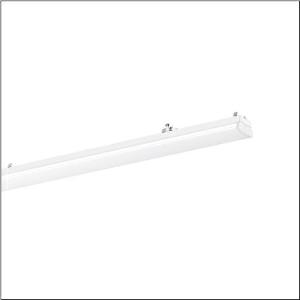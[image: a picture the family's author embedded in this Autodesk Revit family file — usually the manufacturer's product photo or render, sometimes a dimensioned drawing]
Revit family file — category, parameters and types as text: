
# Revit family: licross_r__11_recessed_opal_mo_51tl1ddv4e5g_e7a4
name_source: partatom
category: Lighting Fixtures
units: mm (PartAtom-declared; Revit-internal decimal feet)

## family parameters
Cut with Voids When Loaded = No
Host = Face
Light Source = No
Part Type = Normal
Room Calculation Point = No
Round Connector Dimension = Use Diameter
Shared = No

## types (1)
- --- (1 x LED, 14560 lm, 84.1 W, 4000K)
    Apparent Load = 84 VA
    CIE Flux Codes = 44 73 91 87 100
    Color Rendering = 80
    Color Temperature = 4000K
    Default Elevation = 1800 mm
    Description = Licross® 11 recessed opal MO, luminaire insert, of sheet steel, coil coated, white, length: 2.250mm, width: 76mm, height: 87mm, LED rated luminous flux: 14.560lm, light colour: 840, control gear: DALI 2, with plug, 5-pole, with phase selection, mains connection: 220..240V, AC, 50/60Hz, rated input power: 84W, halogen-free wiring, primary optical cover: cover, of PMMA, light emission: direct with ceiling illumination distribution, primary light characteristic: symmetric, protection rating (complete): IP40, insulation class (complete): insulation class I (protective earthing), certification: CE, ENEC, VDE, UKCA, protection symbol: D if used in an environment without relevant dust loads with corresponding accessories, impact resistance: IK06, permissible ambient temperature for indoor applications: -25..+35°C, corresponds to IFS (International Featured Standards) requirements for safety and quality in the food industry, reducing of maximum allowable ambient temperature of 5°C with ceiling mounting, LABS conformity tested according to VDMA 24364:2018-05, packaging unit: 1 piece
    Height = 83 mm
    Lamp = 1 x LED
    Lamp Light Flux = 14560 lm
    Lamp Power = 84.1 W
    Lamp count = 1
    Length = 2250 mm
    Luminous efficacy = 173 lm/W
    Manufacturer = Siteco
    ModVariant = No
    Model = 51TL1DDV4E5G
    Mounting Place = Ceiling
    Mounting Type = Pendant
    Number of Poles = 1
    OnlyDefault = Yes
    Power Factor = 1
    Product Name = Licross® 11 recessed opal MO
    Product group = luminaire insert
    ProductGroupID = 901
    Protection Class = Protection class I
    Protection Degree = IP 40
    RLX_Detail_Level = 1
    RLX_Emergency_Light_Flux = 0 lm
    RLX_Emergency_Type = 0
    RLX_Emergency_Type_DB = No
    RlxData = <blob elided: 26997 chars, md5=e5545f02>
    Socket = socket
    Standby Power = 0 W
    System Light Flux = 14560 lm
    System Power = 84 W
    Type Comments = factory setting: luminous flux: 100 % | dim-lin: 254 | 378 mA
    Type Image = l_1313666.jpg
    URL = http://relux.com
    VarID = @adj_045449
    Voltage = 0 V
    Weight = 0.00 kg
    Width = 76 mm

## geometry (parser evidence)
native form markers: Blend x4, Sweep x13
no freeform markers — native parametric forms only
